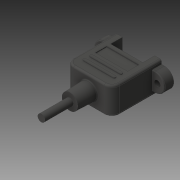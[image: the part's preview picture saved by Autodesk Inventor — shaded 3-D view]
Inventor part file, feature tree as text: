
AUTODESK INVENTOR PART (.ipt)
format: ipt  version: 2016 (Build 200138000, 138)  size: 291,328 bytes
history: native  units: mm
features: sketch x11, extrude x9, fillet x3, mirror x2, plane x1
ambient origin geometry x8: Origin, YZ Plane, XZ Plane, XY Plane, X Axis, Y Axis, Z Axis, Center Point
bodies: Solid1 (feature_tree)
feature tree (26):
  extrude  "Extrusion1"  Depth=26.15mm
  extrude  "Extrusion2"  Depth=14.2mm TaperAngle=0.0deg
  sketch  "Sketch3"  dims[d5=9.9mm d6=6.45mm]
  extrude  "Extrusion3"  Depth=9.9mm
  mirror  "Mirror1"
  extrude  "Extrusion4"  Depth=5.5mm
  extrude  "Extrusion5"  Depth=5.0mm TaperAngle=0.0deg
  extrude  "Extrusion6"  Depth=6.3mm TaperAngle=0.0deg
  sketch  "Sketch8"  dims[d19=10.0mm d20=-0.349066mm d21=3.76mm d22=15.0mm d23=0.0mm d24=12.12mm]
  fillet  "Fillet1"  Radius=9.0mm
  extrude  "Extrusion7"  Depth=12.075mm
  extrude  "Extrusion8"  Depth=15.0mm
  plane  "Work Plane1"
  mirror  "Mirror2"
  fillet  "Fillet2"  Radius=15.0mm
  fillet  "Fillet3"  Radius=12.12mm
  extrude  "Extrusion9"  Depth=1.0mm
  sketch  "Sketch1"  dims[d0=24.15mm d1=26.15mm]
  sketch  "Sketch2"  dims[d2=4.0mm d3=14.2mm d4=0.0mm]
  sketch  "Sketch4"  dims[d7=5.0mm d8=0.0mm d9=5.5mm]
  sketch  "Sketch5"  dims[d10=3.2mm d11=5.0mm d12=0.0mm]
  sketch  "Sketch6"  dims[d13=17.0mm d14=6.3mm d15=0.0mm d16=9.0mm]
  sketch  "Sketch7"  dims[d17=7.1mm d18=12.075mm]
  sketch  "Sketch9"  dims[d25=11.05mm d26=1.0mm]
  sketch  "Sketch10"  dims[d27=17.0mm]
  sketch  "Sketch11"  dims[d28=6.0mm d29=2.0mm d30=0.5mm d31=0.0mm d32=17.0mm d33=1.5mm d34=2.0mm d35=17.0mm d36=1.5mm d37=2.0mm d38=0.75mm d39=0.4mm d40=0.0mm d41=0.5mm d42=0.5mm d43=9.0mm d44=9.0mm d45=4.0mm d46=0.0mm]
